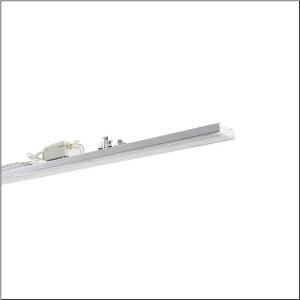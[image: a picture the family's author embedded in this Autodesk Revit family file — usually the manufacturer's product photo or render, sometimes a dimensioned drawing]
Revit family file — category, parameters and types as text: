
# Revit family: licross_r__21_recessed_mo_52te197n48xg_029e
name_source: partatom
category: Lighting Fixtures
units: mm (PartAtom-declared; Revit-internal decimal feet)

## family parameters
Cut with Voids When Loaded = No
Host = Face
Light Source = No
Part Type = Normal
Room Calculation Point = No
Round Connector Dimension = Use Diameter
Shared = No

## types (1)
- Licross® 21 Recessed MO (1 x LED, 8450 lm, 47.9 W, 4000K)
    Apparent Load = 48 VA
    CIE Flux Codes = 55 90 98 100 100
    Color Rendering = 80
    Color Temperature = 4000K
    Default Elevation = 1800 mm
    Description = Licross® 21 Recessed MO, luminaire insert, of sheet steel, galvanised, coil coated, white, length: 1.500mm, width: 66mm, height: 67mm, LED rated luminous flux: 8.450lm, light colour: 840, control gear: ON/OFF, with plug, 3-pole, with phase selection, mains connection: 220..240V, AC, 50/60Hz, rated input power: 48W, halogen-free wiring, primary light control with lens, of plastic, primary optical cover: cover, of PMMA, light emission: direct distribution, primary light characteristic: double asymmetric, protection rating (complete): IP54, insulation class (complete): insulation class I (protective earthing), certification: CE, ENEC, VDE, UKCA, protection symbol: D if used in an environment with non-conductive dust loads with corresponding accessories, impact resistance: IK06, permissible ambient temperature for indoor applications: -35..+40°C, corresponds to IFS (International Featured Standards) requirements for safety and quality in the food industry, reducing of maximum allowable ambient temperature of 5°C with ceiling mounting, LABS conformity tested according to VDMA 24364:2018-05, packaging unit: 1 piece
    Height = 58 mm
    Lamp = 1 x LED
    Lamp Light Flux = 8450 lm
    Lamp Power = 47.9 W
    Lamp count = 1
    Length = 1500 mm
    Luminous efficacy = 176 lm/W
    Manufacturer = Siteco
    ModVariant = No
    Model = 52TE197N48XG
    Mounting Place = Ceiling
    Mounting Type = Pendant
    Number of Poles = 1
    OnlyDefault = Yes
    Power Factor = 1
    Product Name = Licross® 21 Recessed MO
    Product group = luminaire insert
    ProductGroupID = 901
    Protection Class = Protection class I
    Protection Degree = IP 54
    RLX_Detail_Level = 1
    RLX_Emergency_Light_Flux = 0 lm
    RLX_Emergency_Type = 0
    RLX_Emergency_Type_DB = No
    RlxData = <blob elided: 20889 chars, md5=0dc39ec0>
    Socket = socket
    Standby Power = 0 W
    System Light Flux = 8450 lm
    System Power = 48 W
    Type Comments = Product without accessories
    Type Image = l_1296930.jpg
    URL = http://relux.com
    VarID = ---
    Voltage = 0 V
    Weight = 0.00 kg
    Width = 66 mm

## geometry (parser evidence)
native form markers: Blend x4, Sweep x11
no freeform markers — native parametric forms only
